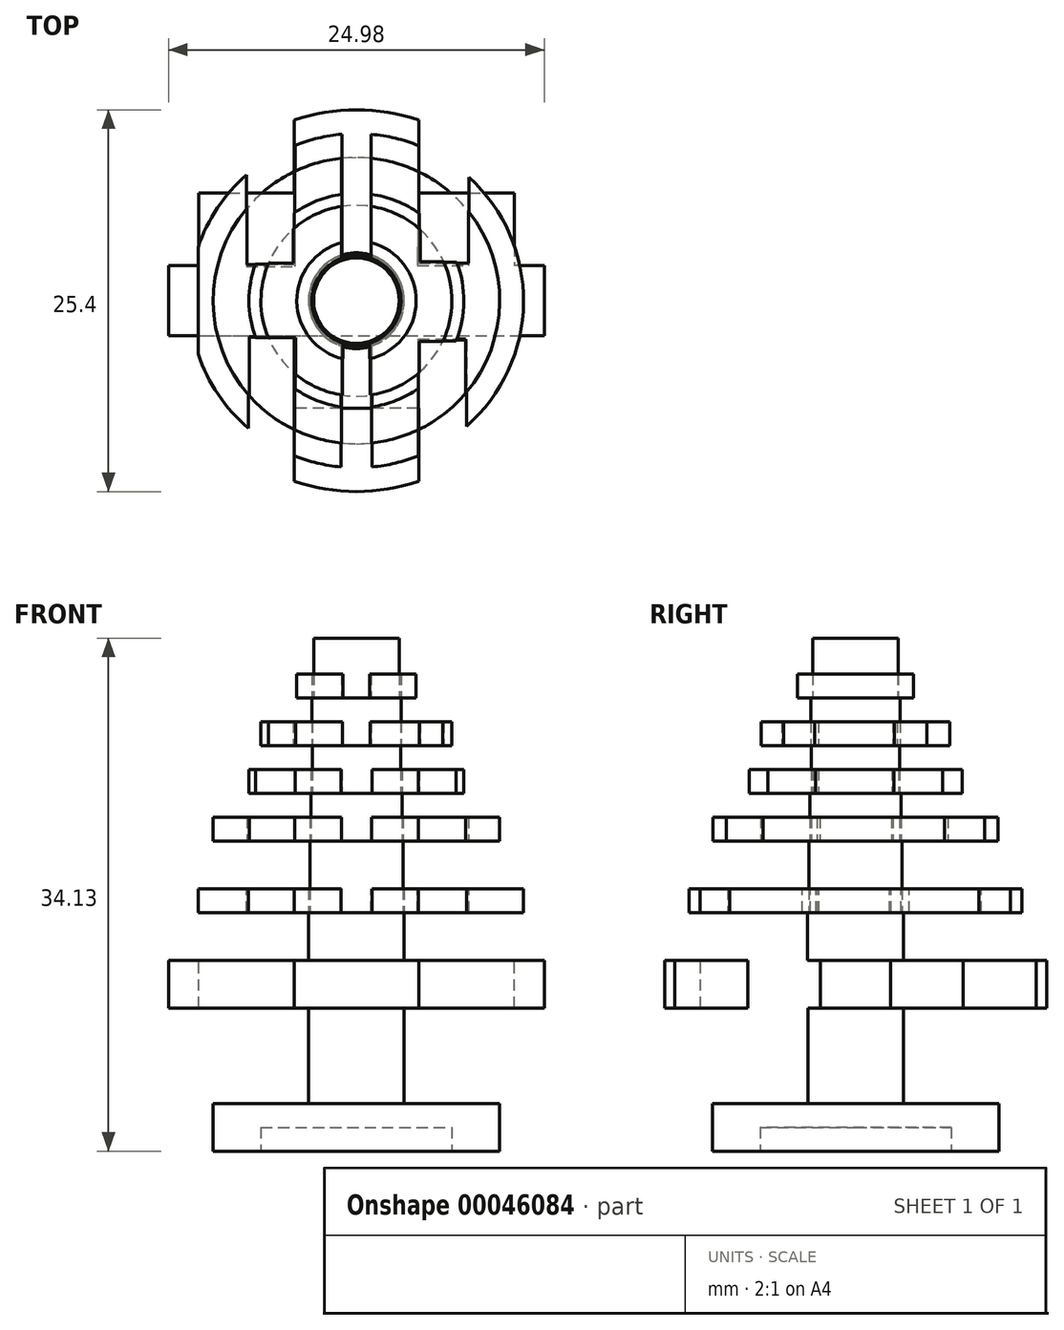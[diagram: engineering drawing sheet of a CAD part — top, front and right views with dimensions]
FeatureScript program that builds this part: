
annotation { "Feature Type Name" : "Feature", "Feature Type Description" : "" }
export const myFeature = defineFeature(function(context is Context, id is Id, definition is map)
    precondition{}
    {
        {
            var Q0;
            Q0=qCreatedBy(makeId("Top.planeOp"),FACE);
            var sketch = newSketch(context, id + "F0", { "sketchPlane" : qUnion([Q0])});
            skCircle(sketch, "E0", {"center": v(0, 0) * mm, "radius": 9.53 * mm});
            skSolve(sketch);
        }
        {
            var Q0;
            Q0=makeQuery(id+"F0.imprint","IMPRINT",FACE,{"disambiguationData":[TD([[makeQuery(id+"F0.imprint","IMPRINT",EDGE,{"derivedFrom":sQuery(id+"F0.wireOp",EDGE,"E0")}),1.0]])]});
            extrude(context, id + "F1", {"entities" : qUnion([Q0]), "depth" : 3.17 * mm});
        }
        {
            var Q0;
            Q0=makeQuery(id+"F1.opExtrude","CAP_FACE",FACE,{"disambiguationData":[OSD([sQuery(id+"F0.wireOp",EDGE,"E0")])],"isStart":false});
            var sketch = newSketch(context, id + "F2", { "sketchPlane" : qUnion([Q0])});
            skCircle(sketch, "E1", {"center": v(0, 0) * mm, "radius": 3.18 * mm});
            skSolve(sketch);
        }
        {
            var Q0;
            Q0=makeQuery(id+"F2.imprint","IMPRINT",FACE,{"disambiguationData":[TD([[makeQuery(id+"F2.imprint","IMPRINT",EDGE,{"derivedFrom":sQuery(id+"F2.wireOp",EDGE,"E1")}),1.0]])]});
            extrude(context, id + "F3", {"entities" : qUnion([Q0]), "depth" : 6.35 * mm});
        }
        {
            var Q0;
            Q0=makeQuery(id+"F1.opExtrude","CAP_FACE",FACE,{"disambiguationData":[OSD([sQuery(id+"F0.wireOp",EDGE,"E0")])],"isStart":true});
            var sketch = newSketch(context, id + "F4", { "sketchPlane" : qUnion([Q0])});
            skCircle(sketch, "E2", {"center": v(0, 0) * mm, "radius": 6.35 * mm});
            skSolve(sketch);
        }
        {
            var Q0;
            Q0=makeQuery(id+"F3.opExtrude","CAP_FACE",FACE,{"disambiguationData":[OSD([sQuery(id+"F2.wireOp",EDGE,"E1")])],"isStart":false});
            var sketch = newSketch(context, id + "F5", { "sketchPlane" : qUnion([Q0])});
            skCircle(sketch, "E3", {"center": v(0, 0) * mm, "radius": 12.7 * mm});
            skSolve(sketch);
        }
        {
            var Q0;
            Q0=makeQuery(id+"F5.imprint","IMPRINT",FACE,{"disambiguationData":[TD([[makeQuery(id+"F5.imprint","IMPRINT",EDGE,{"derivedFrom":makeQuery(id+"F3.opExtrude","CAP_EDGE",EDGE,{"disambiguationData":[OSD([sQuery(id+"F2.wireOp",EDGE,"E1")])],"isStart":false})}),1.0]])]});
            var Q1;
            Q1=makeQuery(id+"F5.imprint","IMPRINT",FACE,{"disambiguationData":[TD([[makeQuery(id+"F5.imprint","IMPRINT",EDGE,{"derivedFrom":sQuery(id+"F5.wireOp",EDGE,"E3")}),1.0]])]});
            extrude(context, id + "F6", {"entities" : qUnion([Q0, Q1]), "operationType" : NewBodyOperationType.ADD, "depth" : 3.17 * mm});
        }
        {
            var Q0;
            Q0=makeQuery(id+"F6.opExtrude","CAP_FACE",FACE,{"disambiguationData":[OSD([sQuery(id+"F5.wireOp",EDGE,"E3")])],"isStart":false});
            var sketch = newSketch(context, id + "F7", { "sketchPlane" : qUnion([Q0])});
            skLineSegment(sketch, "E4", {"start": v(10.49, 7.16) * mm, "end": v(10.49, -7.16) * mm});
            skLineSegment(sketch, "E5", {"start": v(10.49, -2.32) * mm, "end": v(12.49, -2.32) * mm});
            skLineSegment(sketch, "E6", {"start": v(12.49, -2.32) * mm, "end": v(12.49, 2.32) * mm});
            skLineSegment(sketch, "E7", {"start": v(12.49, 2.32) * mm, "end": v(10.49, 2.32) * mm});
            skLineSegment(sketch, "E8", {"start": v(10.49, 2.32) * mm, "end": v(-12.49, 2.32) * mm});
            skLineSegment(sketch, "E9", {"start": v(-12.49, 2.32) * mm, "end": v(-12.49, -2.32) * mm});
            skLineSegment(sketch, "E10", {"start": v(-12.49, -2.32) * mm, "end": v(10.49, -2.32) * mm});
            skLineSegment(sketch, "E11", {"start": v(10.49, -7.16) * mm, "end": v(-10.49, -7.16) * mm});
            skLineSegment(sketch, "E12", {"start": v(-10.49, -7.16) * mm, "end": v(-10.49, 7.16) * mm});
            skLineSegment(sketch, "E13", {"start": v(-10.49, 7.16) * mm, "end": v(10.49, 7.16) * mm});
            skLineSegment(sketch, "E14", {"start": v(-10.49, 2.32) * mm, "end": v(-12.49, 2.32) * mm});
            skLineSegment(sketch, "E15", {"start": v(-10.49, 7.16) * mm, "end": v(-7.31, 7.16) * mm});
            skLineSegment(sketch, "E16", {"start": v(-7.31, 7.16) * mm, "end": v(-7.31, 10.38) * mm});
            skLineSegment(sketch, "E17", {"start": v(-4.14, 12) * mm, "end": v(-4.14, 7.16) * mm});
            skLineSegment(sketch, "E18", {"start": v(-7.31, 7.16) * mm, "end": v(-4.14, 7.16) * mm});
            skLineSegment(sketch, "E19", {"start": v(10.49, 7.16) * mm, "end": v(7.31, 7.16) * mm});
            skLineSegment(sketch, "E20", {"start": v(7.31, 7.16) * mm, "end": v(7.31, 10.38) * mm});
            skLineSegment(sketch, "E21", {"start": v(7.31, 7.16) * mm, "end": v(4.14, 7.16) * mm});
            skLineSegment(sketch, "E22", {"start": v(4.14, 7.16) * mm, "end": v(4.14, 12) * mm});
            skLineSegment(sketch, "E23", {"start": v(-4.14, 7.16) * mm, "end": v(-0.96, 7.16) * mm});
            skLineSegment(sketch, "E24", {"start": v(-0.96, 7.16) * mm, "end": v(-0.96, 12.66) * mm});
            skLineSegment(sketch, "E25", {"start": v(4.14, 7.16) * mm, "end": v(0.96, 7.16) * mm});
            skLineSegment(sketch, "E26", {"start": v(0.96, 7.16) * mm, "end": v(0.96, 12.66) * mm});
            skLineSegment(sketch, "E27", {"start": v(-10.49, -7.16) * mm, "end": v(-7.31, -7.16) * mm});
            skLineSegment(sketch, "E28", {"start": v(-7.31, -7.16) * mm, "end": v(-7.31, -10.38) * mm});
            skLineSegment(sketch, "E29", {"start": v(-7.31, -7.16) * mm, "end": v(-4.14, -7.16) * mm});
            skLineSegment(sketch, "E30", {"start": v(-4.14, -7.16) * mm, "end": v(-4.14, -12) * mm});
            skLineSegment(sketch, "E31", {"start": v(-4.14, -7.16) * mm, "end": v(-0.96, -7.16) * mm});
            skLineSegment(sketch, "E32", {"start": v(-0.96, -7.16) * mm, "end": v(-0.96, -12.66) * mm});
            skLineSegment(sketch, "E33", {"start": v(10.49, -7.16) * mm, "end": v(7.31, -7.16) * mm});
            skLineSegment(sketch, "E34", {"start": v(7.31, -7.16) * mm, "end": v(7.31, -10.38) * mm});
            skLineSegment(sketch, "E35", {"start": v(7.31, -7.16) * mm, "end": v(4.14, -7.16) * mm});
            skLineSegment(sketch, "E36", {"start": v(4.14, -7.16) * mm, "end": v(4.14, -12) * mm});
            skLineSegment(sketch, "E37", {"start": v(4.14, -7.16) * mm, "end": v(0.96, -7.16) * mm});
            skLineSegment(sketch, "E38", {"start": v(0.96, -7.16) * mm, "end": v(0.96, -12.66) * mm});
            skLineSegment(sketch, "E39", {"start": v(-0.96, 7.16) * mm, "end": v(-0.96, 2.32) * mm});
            skLineSegment(sketch, "E40", {"start": v(-0.96, 2.32) * mm, "end": v(-4.14, 2.32) * mm});
            skLineSegment(sketch, "E41", {"start": v(-4.14, 2.32) * mm, "end": v(-4.14, 7.16) * mm});
            skLineSegment(sketch, "E42", {"start": v(-4.14, 2.32) * mm, "end": v(-7.31, 2.32) * mm});
            skLineSegment(sketch, "E43", {"start": v(-7.31, 2.32) * mm, "end": v(-7.31, 7.16) * mm});
            skLineSegment(sketch, "E44", {"start": v(-7.31, 2.32) * mm, "end": v(-10.49, 2.32) * mm});
            skLineSegment(sketch, "E45", {"start": v(0.96, 7.16) * mm, "end": v(0.96, 2.32) * mm});
            skLineSegment(sketch, "E46", {"start": v(0.96, 2.32) * mm, "end": v(4.14, 2.32) * mm});
            skLineSegment(sketch, "E47", {"start": v(4.14, 2.32) * mm, "end": v(4.14, 7.16) * mm});
            skLineSegment(sketch, "E48", {"start": v(4.14, 2.32) * mm, "end": v(7.31, 2.32) * mm});
            skLineSegment(sketch, "E49", {"start": v(7.31, 2.32) * mm, "end": v(7.31, 7.16) * mm});
            skLineSegment(sketch, "E50", {"start": v(7.31, 2.32) * mm, "end": v(10.49, 2.32) * mm});
            skLineSegment(sketch, "E51", {"start": v(7.31, -7.16) * mm, "end": v(7.31, -2.32) * mm});
            skLineSegment(sketch, "E52", {"start": v(4.14, -7.16) * mm, "end": v(4.14, -2.32) * mm});
            skLineSegment(sketch, "E53", {"start": v(0.96, -7.16) * mm, "end": v(0.96, -2.32) * mm});
            skLineSegment(sketch, "E54", {"start": v(-0.96, -7.16) * mm, "end": v(-0.96, -2.32) * mm});
            skLineSegment(sketch, "E55", {"start": v(-4.14, -7.16) * mm, "end": v(-4.14, -2.32) * mm});
            skLineSegment(sketch, "E56", {"start": v(-7.31, -7.16) * mm, "end": v(-7.31, -2.32) * mm});
            skSolve(sketch);
        }
        {
            var Q0;
            {var subQ1=sQuery(id+"F7.wireOp",EDGE,"E9");Q0=makeQuery(id+"F7.imprint","IMPRINT",FACE,{"disambiguationData":[TD([[makeQuery(id+"F7.imprint","IMPRINT",EDGE,{"derivedFrom":subQ1}),-1.0]])]});}
            var Q1;
            {var subQ3=sQuery(id+"F7.wireOp",EDGE,"E14");Q1=makeQuery(id+"F7.imprint","IMPRINT",FACE,{"disambiguationData":[TD([[makeQuery(id+"F7.imprint","IMPRINT",EDGE,{"derivedFrom":subQ3}),-1.0]])]});}
            var Q2;
            {var subQ1=sQuery(id+"F7.wireOp",EDGE,"E12");var subQ3=sQuery(id+"F7.wireOp",EDGE,"E10");var subQ5=makeQuery(id+"F7.imprint","INTERSECT",VERTEX,{"derivedFrom":[subQ3,subQ1]});Q2=makeQuery(id+"F7.imprint","IMPRINT",FACE,{"disambiguationData":[TD([[makeQuery(id+"F7.imprint","IMPRINT",EDGE,{"disambiguationData":[TD([[subQ5,1.0]])],"derivedFrom":subQ3}),-1.0]])]});}
            var Q3;
            {var subQ2=sQuery(id+"F7.wireOp",EDGE,"E28");Q3=makeQuery(id+"F7.imprint","IMPRINT",FACE,{"disambiguationData":[TD([[makeQuery(id+"F7.imprint","IMPRINT",EDGE,{"derivedFrom":subQ2}),1.0]])]});}
            var Q4;
            Q4=makeQuery(id+"F7.imprint","IMPRINT",FACE,{"disambiguationData":[TD([[makeQuery(id+"F7.imprint","IMPRINT",EDGE,{"derivedFrom":sQuery(id+"F7.wireOp",EDGE,"E29")}),1.0]])]});
            var Q5;
            Q5=makeQuery(id+"F7.imprint","IMPRINT",FACE,{"disambiguationData":[TD([[makeQuery(id+"F7.imprint","IMPRINT",EDGE,{"derivedFrom":sQuery(id+"F7.wireOp",EDGE,"E18")}),-1.0]])]});
            var Q6;
            {var subQ2=sQuery(id+"F7.wireOp",EDGE,"E16");Q6=makeQuery(id+"F7.imprint","IMPRINT",FACE,{"disambiguationData":[TD([[makeQuery(id+"F7.imprint","IMPRINT",EDGE,{"derivedFrom":subQ2}),-1.0]])]});}
            var Q7;
            Q7=makeQuery(id+"F7.imprint","IMPRINT",FACE,{"disambiguationData":[TD([[makeQuery(id+"F7.imprint","IMPRINT",EDGE,{"derivedFrom":sQuery(id+"F7.wireOp",EDGE,"E13")}),1.0]])]});
            var Q8;
            Q8=makeQuery(id+"F7.imprint","IMPRINT",FACE,{"disambiguationData":[TD([[makeQuery(id+"F7.imprint","IMPRINT",EDGE,{"derivedFrom":sQuery(id+"F7.wireOp",EDGE,"E8")}),-1.0]])]});
            var Q9;
            Q9=makeQuery(id+"F7.imprint","IMPRINT",FACE,{"disambiguationData":[TD([[makeQuery(id+"F7.imprint","IMPRINT",EDGE,{"derivedFrom":sQuery(id+"F7.wireOp",EDGE,"E11")}),-1.0]])]});
            var Q10;
            Q10=makeQuery(id+"F7.imprint","IMPRINT",FACE,{"disambiguationData":[TD([[makeQuery(id+"F7.imprint","IMPRINT",EDGE,{"derivedFrom":sQuery(id+"F7.wireOp",EDGE,"E11")}),1.0]])]});
            var Q11;
            {var subQ2=sQuery(id+"F7.wireOp",EDGE,"E34");Q11=makeQuery(id+"F7.imprint","IMPRINT",FACE,{"disambiguationData":[TD([[makeQuery(id+"F7.imprint","IMPRINT",EDGE,{"derivedFrom":subQ2}),-1.0]])]});}
            var Q12;
            Q12=makeQuery(id+"F7.imprint","IMPRINT",FACE,{"disambiguationData":[TD([[makeQuery(id+"F7.imprint","IMPRINT",EDGE,{"derivedFrom":sQuery(id+"F7.wireOp",EDGE,"E35")}),-1.0]])]});
            var Q13;
            {var subQ1=sQuery(id+"F7.wireOp",EDGE,"E5");Q13=makeQuery(id+"F7.imprint","IMPRINT",FACE,{"disambiguationData":[TD([[makeQuery(id+"F7.imprint","IMPRINT",EDGE,{"derivedFrom":subQ1}),-1.0]])]});}
            var Q14;
            {var subQ0=sQuery(id+"F7.wireOp",EDGE,"E7");Q14=makeQuery(id+"F7.imprint","IMPRINT",FACE,{"disambiguationData":[TD([[makeQuery(id+"F7.imprint","IMPRINT",EDGE,{"derivedFrom":subQ0}),-1.0]])]});}
            var Q15;
            Q15=makeQuery(id+"F7.imprint","IMPRINT",FACE,{"disambiguationData":[TD([[makeQuery(id+"F7.imprint","IMPRINT",EDGE,{"derivedFrom":sQuery(id+"F7.wireOp",EDGE,"E21")}),1.0]])]});
            var Q16;
            {var subQ2=sQuery(id+"F7.wireOp",EDGE,"E20");Q16=makeQuery(id+"F7.imprint","IMPRINT",FACE,{"disambiguationData":[TD([[makeQuery(id+"F7.imprint","IMPRINT",EDGE,{"derivedFrom":subQ2}),1.0]])]});}
            var Q17;
            {var subQ1=sQuery(id+"F7.wireOp",EDGE,"E6");Q17=makeQuery(id+"F7.imprint","IMPRINT",FACE,{"disambiguationData":[TD([[makeQuery(id+"F7.imprint","IMPRINT",EDGE,{"derivedFrom":subQ1}),-1.0]])]});}
            extrude(context, id + "F8", {"entities" : qUnion([Q0, Q1, Q2, Q3, Q4, Q5, Q6, Q7, Q8, Q9, Q10, Q11, Q12, Q13, Q14, Q15, Q16, Q17]), "operationType" : NewBodyOperationType.REMOVE, "oppositeDirection" : true, "depth" : 3.17 * mm});
        }
        {
            var Q0;
            Q0=makeQuery(id+"F7.imprint","IMPRINT",FACE,{"disambiguationData":[TD([[makeQuery(id+"F7.imprint","IMPRINT",EDGE,{"derivedFrom":sQuery(id+"F7.wireOp",EDGE,"E8")}),1.0]])]});
            var sketch = newSketch(context, id + "F9", { "sketchPlane" : qUnion([Q0])});
            skCircle(sketch, "E57", {"center": v(0, 0) * mm, "radius": 3.18 * mm});
            skSolve(sketch);
        }
        {
            var Q0;
            Q0 = qSketchRegion(id + "F9", true);
            extrude(context, id + "F10", {"entities" : qUnion([Q0]), "operationType" : NewBodyOperationType.ADD, "depth" : 3.17 * mm});
        }
        {
            var Q0;
            Q0=makeQuery(id+"F10.opExtrude","CAP_FACE",FACE,{"disambiguationData":[OSD([sQuery(id+"F9.wireOp",EDGE,"E57")])],"isStart":false});
            var sketch = newSketch(context, id + "F11", { "sketchPlane" : qUnion([Q0])});
            skCircle(sketch, "E58", {"center": v(0, 0) * mm, "radius": 11.11 * mm});
            skSolve(sketch);
        }
        {
            var Q0;
            Q0=makeQuery(id+"F11.imprint","IMPRINT",FACE,{"disambiguationData":[TD([[makeQuery(id+"F11.imprint","IMPRINT",EDGE,{"derivedFrom":sQuery(id+"F11.wireOp",EDGE,"E58")}),1.0]])]});
            extrude(context, id + "F12", {"entities" : qUnion([Q0]), "depth" : 1.59 * mm});
        }
        {
            var Q0;
            Q0=makeQuery(id+"F12.opExtrude","CAP_FACE",FACE,{"disambiguationData":[OSD([sQuery(id+"F9.wireOp",EDGE,"E57"),sQuery(id+"F11.wireOp",EDGE,"E58")])],"isStart":false});
            var sketch = newSketch(context, id + "F13", { "sketchPlane" : qUnion([Q0])});
            skLineSegment(sketch, "E59", {"start": v(-0.97, 3.03) * mm, "end": v(-0.97, 11.07) * mm});
            skLineSegment(sketch, "E60", {"start": v(-0.97, 11.07) * mm, "end": v(0.97, 11.07) * mm});
            skLineSegment(sketch, "E61", {"start": v(0.97, 11.07) * mm, "end": v(0.97, 3.03) * mm});
            skLineSegment(sketch, "E62", {"start": v(0.97, 3.03) * mm, "end": v(-0.97, 3.03) * mm});
            skLineSegment(sketch, "E63", {"start": v(4.06, 2.35) * mm, "end": v(7.5, 2.35) * mm});
            skLineSegment(sketch, "E64", {"start": v(7.5, 2.35) * mm, "end": v(7.5, 8.2) * mm});
            skLineSegment(sketch, "E65", {"start": v(7.5, 8.2) * mm, "end": v(4.16, 10.3) * mm});
            skLineSegment(sketch, "E66", {"start": v(4.16, 10.3) * mm, "end": v(4.06, 2.35) * mm});
            skLineSegment(sketch, "E67", {"start": v(10.59, 3.37) * mm, "end": v(10.59, -3.37) * mm});
            skLineSegment(sketch, "E68", {"start": v(-10.53, 3.55) * mm, "end": v(-10.53, -3.55) * mm});
            skLineSegment(sketch, "E69", {"start": v(-7.31, 8.37) * mm, "end": v(-7.31, 2.26) * mm});
            skLineSegment(sketch, "E70", {"start": v(-7.31, 2.26) * mm, "end": v(-4.08, 2.26) * mm});
            skLineSegment(sketch, "E71", {"start": v(-4.08, 2.26) * mm, "end": v(-4.08, 10.34) * mm});
            skLineSegment(sketch, "E72", {"start": v(-4.08, 10.34) * mm, "end": v(-7.31, 8.37) * mm});
            skLineSegment(sketch, "E73", {"start": v(-7.17, -2.44) * mm, "end": v(-7.17, -8.49) * mm});
            skLineSegment(sketch, "E74", {"start": v(-7.17, -8.49) * mm, "end": v(-4.13, -10.32) * mm});
            skLineSegment(sketch, "E75", {"start": v(-4.13, -10.32) * mm, "end": v(-4.13, -2.48) * mm});
            skLineSegment(sketch, "E76", {"start": v(-4.13, -2.48) * mm, "end": v(-7.17, -2.44) * mm});
            skLineSegment(sketch, "E77", {"start": v(-1.04, -2.53) * mm, "end": v(-1.04, -11.06) * mm});
            skLineSegment(sketch, "E78", {"start": v(-1.04, -11.06) * mm, "end": v(1.04, -11.06) * mm});
            skLineSegment(sketch, "E79", {"start": v(1.04, -11.06) * mm, "end": v(1.04, -3) * mm});
            skLineSegment(sketch, "E80", {"start": v(1.04, -3) * mm, "end": v(-1.04, -3) * mm});
            skLineSegment(sketch, "E81", {"start": v(4.11, -10.32) * mm, "end": v(4.11, -2.61) * mm});
            skLineSegment(sketch, "E82", {"start": v(4.11, -2.61) * mm, "end": v(7.32, -2.61) * mm});
            skLineSegment(sketch, "E83", {"start": v(7.32, -2.61) * mm, "end": v(7.32, -8.36) * mm});
            skLineSegment(sketch, "E84", {"start": v(7.32, -8.36) * mm, "end": v(4.11, -10.32) * mm});
            skSolve(sketch);
        }
        {
            var Q0;
            {var subQ1=sQuery(id+"F13.wireOp",EDGE,"E78");Q0=makeQuery(id+"F13.imprint","IMPRINT",FACE,{"disambiguationData":[TD([[makeQuery(id+"F13.imprint","IMPRINT",EDGE,{"derivedFrom":subQ1}),1.0]])]});}
            var Q1;
            Q1=makeQuery(id+"F13.imprint","IMPRINT",FACE,{"disambiguationData":[TD([[makeQuery(id+"F13.imprint","IMPRINT",EDGE,{"derivedFrom":sQuery(id+"F13.wireOp",EDGE,"E81")}),-1.0]])]});
            var Q2;
            Q2=makeQuery(id+"F13.imprint","IMPRINT",FACE,{"disambiguationData":[TD([[makeQuery(id+"F13.imprint","IMPRINT",EDGE,{"derivedFrom":sQuery(id+"F13.wireOp",EDGE,"E73")}),1.0]])]});
            var Q3;
            {var subQ1=sQuery(id+"F13.wireOp",EDGE,"E68");Q3=makeQuery(id+"F13.imprint","IMPRINT",FACE,{"disambiguationData":[TD([[makeQuery(id+"F13.imprint","IMPRINT",EDGE,{"derivedFrom":subQ1}),-1.0]])]});}
            var Q4;
            Q4=makeQuery(id+"F13.imprint","IMPRINT",FACE,{"disambiguationData":[TD([[makeQuery(id+"F13.imprint","IMPRINT",EDGE,{"derivedFrom":sQuery(id+"F13.wireOp",EDGE,"E69")}),1.0]])]});
            var Q5;
            {var subQ3=sQuery(id+"F13.wireOp",EDGE,"E59");Q5=makeQuery(id+"F13.imprint","IMPRINT",FACE,{"disambiguationData":[TD([[makeQuery(id+"F13.imprint","IMPRINT",EDGE,{"derivedFrom":subQ3}),-1.0]])]});}
            var Q6;
            Q6=makeQuery(id+"F13.imprint","IMPRINT",FACE,{"disambiguationData":[TD([[makeQuery(id+"F13.imprint","IMPRINT",EDGE,{"derivedFrom":sQuery(id+"F13.wireOp",EDGE,"E63")}),1.0]])]});
            var Q7;
            {var subQ1=sQuery(id+"F13.wireOp",EDGE,"E65");Q7=makeQuery(id+"F13.imprint","IMPRINT",FACE,{"disambiguationData":[TD([[makeQuery(id+"F13.imprint","IMPRINT",EDGE,{"derivedFrom":subQ1}),-1.0]])]});}
            var Q8;
            {var subQ1=sQuery(id+"F13.wireOp",EDGE,"E78");Q8=makeQuery(id+"F13.imprint","IMPRINT",FACE,{"disambiguationData":[TD([[makeQuery(id+"F13.imprint","IMPRINT",EDGE,{"derivedFrom":subQ1}),-1.0]])]});}
            var Q9;
            {var subQ1=sQuery(id+"F13.wireOp",EDGE,"E84");Q9=makeQuery(id+"F13.imprint","IMPRINT",FACE,{"disambiguationData":[TD([[makeQuery(id+"F13.imprint","IMPRINT",EDGE,{"derivedFrom":subQ1}),1.0]])]});}
            var Q10;
            {var subQ1=sQuery(id+"F13.wireOp",EDGE,"E72");Q10=makeQuery(id+"F13.imprint","IMPRINT",FACE,{"disambiguationData":[TD([[makeQuery(id+"F13.imprint","IMPRINT",EDGE,{"derivedFrom":subQ1}),-1.0]])]});}
            var Q11;
            {var subQ1=sQuery(id+"F13.wireOp",EDGE,"E60");Q11=makeQuery(id+"F13.imprint","IMPRINT",FACE,{"disambiguationData":[TD([[makeQuery(id+"F13.imprint","IMPRINT",EDGE,{"derivedFrom":subQ1}),1.0]])]});}
            extrude(context, id + "F14", {"entities" : qUnion([Q0, Q1, Q2, Q3, Q4, Q5, Q6, Q7, Q8, Q9, Q10, Q11]), "operationType" : NewBodyOperationType.REMOVE, "oppositeDirection" : true, "depth" : 1.59 * mm});
        }
        {
            var Q0;
            Q0=makeQuery(id+"F4.imprint","IMPRINT",FACE,{"disambiguationData":[TD([[makeQuery(id+"F4.imprint","IMPRINT",EDGE,{"derivedFrom":sQuery(id+"F4.wireOp",EDGE,"E2")}),1.0]])]});
            extrude(context, id + "F15", {"entities" : qUnion([Q0]), "operationType" : NewBodyOperationType.REMOVE, "oppositeDirection" : true, "depth" : 1.59 * mm});
        }
        {
            var Q0;
            Q0=makeQuery(id+"F10.opExtrude","CAP_FACE",FACE,{"disambiguationData":[OSD([sQuery(id+"F9.wireOp",EDGE,"E57")])],"isStart":false});
            var sketch = newSketch(context, id + "F16", { "sketchPlane" : qUnion([Q0])});
            skCircle(sketch, "E85", {"center": v(0, 0) * mm, "radius": 3.1 * mm});
            skSolve(sketch);
        }
        {
            var Q0;
            Q0=makeQuery(id+"F16.imprint","IMPRINT",FACE,{"disambiguationData":[TD([[makeQuery(id+"F16.imprint","IMPRINT",EDGE,{"derivedFrom":sQuery(id+"F16.wireOp",EDGE,"E85")}),1.0]])]});
            extrude(context, id + "F17", {"entities" : qUnion([Q0]), "depth" : 4.76 * mm});
        }
        {
            var Q0;
            {var subQ0=sQuery(id+"F11.wireOp",EDGE,"E58");Q0=makeQuery(id+"F14.boolean.opBoolean","SPLIT",FACE,{"disambiguationData":[TD([makeQuery(id+"F14.opExtrude","SWEPT_FACE",FACE,{"disambiguationData":[OSD([sQuery(id+"F13.wireOp",EDGE,"E74")])]})])],"derivedFrom":makeQuery(id+"F12.opExtrude","CAP_FACE",FACE,{"disambiguationData":[OSD([sQuery(id+"F9.wireOp",EDGE,"E57"),subQ0])],"isStart":false})});}
            extrude(context, id + "F18", {"entities" : qUnion([Q0]), "operationType" : NewBodyOperationType.REMOVE, "oppositeDirection" : true, "depth" : 25.4 * mm});
        }
        {
            var Q0;
            Q0=makeQuery(id+"F17.opExtrude","CAP_FACE",FACE,{"disambiguationData":[OSD([sQuery(id+"F16.wireOp",EDGE,"E85")])],"isStart":false});
            var sketch = newSketch(context, id + "F19", { "sketchPlane" : qUnion([Q0])});
            skCircle(sketch, "E86", {"center": v(0, 0) * mm, "radius": 9.53 * mm});
            skLineSegment(sketch, "E87", {"start": v(-0.98, 9.47) * mm, "end": v(-0.98, 2.94) * mm});
            skLineSegment(sketch, "E88", {"start": v(-0.98, 2.94) * mm, "end": v(0.98, 2.94) * mm});
            skLineSegment(sketch, "E89", {"start": v(0.98, 2.94) * mm, "end": v(0.98, 9.47) * mm});
            skLineSegment(sketch, "E90", {"start": v(0.98, 9.47) * mm, "end": v(-0.98, 9.47) * mm});
            skLineSegment(sketch, "E91", {"start": v(4.15, 8.57) * mm, "end": v(4.15, 2.48) * mm});
            skLineSegment(sketch, "E92", {"start": v(4.15, 2.48) * mm, "end": v(7.46, 2.48) * mm});
            skLineSegment(sketch, "E93", {"start": v(7.46, 2.48) * mm, "end": v(7.46, 5.92) * mm});
            skLineSegment(sketch, "E94", {"start": v(-4.1, 8.6) * mm, "end": v(-4.1, 2.39) * mm});
            skLineSegment(sketch, "E95", {"start": v(-4.1, 2.39) * mm, "end": v(-7.28, 2.39) * mm});
            skLineSegment(sketch, "E96", {"start": v(-7.28, 2.39) * mm, "end": v(-7.28, 6.14) * mm});
            skLineSegment(sketch, "E97", {"start": v(-7.12, -6.32) * mm, "end": v(-7.12, -2.38) * mm});
            skLineSegment(sketch, "E98", {"start": v(-7.12, -2.38) * mm, "end": v(-4.11, -2.38) * mm});
            skLineSegment(sketch, "E99", {"start": v(-4.11, -2.38) * mm, "end": v(-4.11, -8.6) * mm});
            skLineSegment(sketch, "E100", {"start": v(-1, -9.47) * mm, "end": v(-1, -2.93) * mm});
            skLineSegment(sketch, "E101", {"start": v(-1, -2.93) * mm, "end": v(1, -2.93) * mm});
            skLineSegment(sketch, "E102", {"start": v(1, -2.93) * mm, "end": v(1, -9.47) * mm});
            skLineSegment(sketch, "E103", {"start": v(4.11, -8.6) * mm, "end": v(4.11, -2.57) * mm});
            skLineSegment(sketch, "E104", {"start": v(4.11, -2.57) * mm, "end": v(7.27, -2.57) * mm});
            skLineSegment(sketch, "E105", {"start": v(7.27, -2.57) * mm, "end": v(7.27, -6.15) * mm});
            skSolve(sketch);
        }
        {
            var Q0;
            {var subQ5=sQuery(id+"F19.wireOp",EDGE,"E89");Q0=makeQuery(id+"F19.imprint","IMPRINT",FACE,{"disambiguationData":[TD([[makeQuery(id+"F19.imprint","IMPRINT",EDGE,{"derivedFrom":subQ5}),-1.0]])]});}
            var Q1;
            {var subQ5=sQuery(id+"F19.wireOp",EDGE,"E87");Q1=makeQuery(id+"F19.imprint","IMPRINT",FACE,{"disambiguationData":[TD([[makeQuery(id+"F19.imprint","IMPRINT",EDGE,{"derivedFrom":subQ5}),-1.0]])]});}
            extrude(context, id + "F20", {"entities" : qUnion([Q0, Q1]), "depth" : 1.59 * mm});
        }
        {
            var Q0;
            Q0=makeQuery(id+"F17.opExtrude","CAP_FACE",FACE,{"disambiguationData":[OSD([sQuery(id+"F16.wireOp",EDGE,"E85")])],"isStart":false});
            var sketch = newSketch(context, id + "F21", { "sketchPlane" : qUnion([Q0])});
            skCircle(sketch, "E106", {"center": v(0, 0) * mm, "radius": 3.04 * mm});
            skSolve(sketch);
        }
        {
            var Q0;
            Q0=makeQuery(id+"F21.imprint","IMPRINT",FACE,{"disambiguationData":[TD([[makeQuery(id+"F21.imprint","IMPRINT",EDGE,{"derivedFrom":sQuery(id+"F21.wireOp",EDGE,"E106")}),1.0]])]});
            extrude(context, id + "F22", {"entities" : qUnion([Q0]), "operationType" : NewBodyOperationType.ADD, "depth" : 3.17 * mm});
        }
        {
            var Q0;
            Q0=makeQuery(id+"F22.opExtrude","CAP_FACE",FACE,{"disambiguationData":[OSD([sQuery(id+"F21.wireOp",EDGE,"E106")])],"isStart":false});
            var sketch = newSketch(context, id + "F23", { "sketchPlane" : qUnion([Q0])});
            skCircle(sketch, "E107", {"center": v(0, 0) * mm, "radius": 7.14 * mm});
            skLineSegment(sketch, "E108", {"start": v(-4.14, 5.82) * mm, "end": v(-4.14, 2.42) * mm});
            skLineSegment(sketch, "E109", {"start": v(-4.14, 2.42) * mm, "end": v(-6.72, 2.42) * mm});
            skLineSegment(sketch, "E110", {"start": v(-0.97, 7.08) * mm, "end": v(-0.97, 2.88) * mm});
            skLineSegment(sketch, "E111", {"start": v(-0.97, 2.88) * mm, "end": v(0.97, 2.88) * mm});
            skLineSegment(sketch, "E112", {"start": v(0.97, 2.88) * mm, "end": v(0.97, 7.08) * mm});
            skLineSegment(sketch, "E113", {"start": v(4.18, 5.8) * mm, "end": v(4.18, 2.55) * mm});
            skLineSegment(sketch, "E114", {"start": v(4.18, 2.55) * mm, "end": v(6.67, 2.55) * mm});
            skLineSegment(sketch, "E115", {"start": v(4.13, -5.83) * mm, "end": v(4.13, -2.67) * mm});
            skLineSegment(sketch, "E116", {"start": v(4.13, -2.67) * mm, "end": v(6.63, -2.67) * mm});
            skLineSegment(sketch, "E117", {"start": v(1.03, -7.07) * mm, "end": v(1.03, -2.86) * mm});
            skLineSegment(sketch, "E118", {"start": v(1.03, -2.86) * mm, "end": v(-1.03, -2.86) * mm});
            skLineSegment(sketch, "E119", {"start": v(-1.03, -2.86) * mm, "end": v(-1.03, -7.07) * mm});
            skLineSegment(sketch, "E120", {"start": v(-4.08, -5.86) * mm, "end": v(-4.08, -2.45) * mm});
            skLineSegment(sketch, "E121", {"start": v(-4.08, -2.45) * mm, "end": v(-6.71, -2.45) * mm});
            skSolve(sketch);
        }
        {
            var Q0;
            {var subQ0=sQuery(id+"F23.wireOp",EDGE,"E108");Q0=makeQuery(id+"F23.imprint","IMPRINT",FACE,{"disambiguationData":[TD([[makeQuery(id+"F23.imprint","IMPRINT",EDGE,{"derivedFrom":subQ0}),1.0]])]});}
            var Q1;
            {var subQ0=sQuery(id+"F23.wireOp",EDGE,"E112");Q1=makeQuery(id+"F23.imprint","IMPRINT",FACE,{"disambiguationData":[TD([[makeQuery(id+"F23.imprint","IMPRINT",EDGE,{"derivedFrom":subQ0}),-1.0]])]});}
            extrude(context, id + "F24", {"entities" : qUnion([Q0, Q1]), "depth" : 1.59 * mm});
        }
        {
            var Q0;
            Q0=makeQuery(id+"F22.opExtrude","CAP_FACE",FACE,{"disambiguationData":[OSD([sQuery(id+"F21.wireOp",EDGE,"E106")])],"isStart":false});
            var sketch = newSketch(context, id + "F25", { "sketchPlane" : qUnion([Q0])});
            skCircle(sketch, "E122", {"center": v(0, 0) * mm, "radius": 2.94 * mm});
            skSolve(sketch);
        }
        {
            var Q0;
            Q0=makeQuery(id+"F25.imprint","IMPRINT",FACE,{"disambiguationData":[TD([[makeQuery(id+"F25.imprint","IMPRINT",EDGE,{"derivedFrom":sQuery(id+"F25.wireOp",EDGE,"E122")}),1.0]])]});
            extrude(context, id + "F26", {"entities" : qUnion([Q0]), "operationType" : NewBodyOperationType.ADD, "depth" : 3.17 * mm});
        }
        {
            var Q0;
            Q0=makeQuery(id+"F26.opExtrude","CAP_FACE",FACE,{"disambiguationData":[OSD([sQuery(id+"F25.wireOp",EDGE,"E122")])],"isStart":false});
            var sketch = newSketch(context, id + "F27", { "sketchPlane" : qUnion([Q0])});
            skCircle(sketch, "E123", {"center": v(0, 0) * mm, "radius": 6.35 * mm});
            skLineSegment(sketch, "E124", {"start": v(-0.98, 6.27) * mm, "end": v(-0.98, 2.77) * mm});
            skLineSegment(sketch, "E125", {"start": v(-0.98, 2.77) * mm, "end": v(0.98, 2.77) * mm});
            skLineSegment(sketch, "E126", {"start": v(0.98, 2.77) * mm, "end": v(0.98, 6.27) * mm});
            skLineSegment(sketch, "E127", {"start": v(4.23, 4.73) * mm, "end": v(4.23, 2.58) * mm});
            skLineSegment(sketch, "E128", {"start": v(4.23, 2.58) * mm, "end": v(5.8, 2.58) * mm});
            skLineSegment(sketch, "E129", {"start": v(5.85, -2.7) * mm, "end": v(4.19, -2.7) * mm});
            skLineSegment(sketch, "E130", {"start": v(4.19, -2.7) * mm, "end": v(4.19, -4.99) * mm});
            skLineSegment(sketch, "E131", {"start": v(-0.92, -6.28) * mm, "end": v(-0.92, -2.8) * mm});
            skLineSegment(sketch, "E132", {"start": v(-0.92, -2.8) * mm, "end": v(0.92, -2.8) * mm});
            skLineSegment(sketch, "E133", {"start": v(0.92, -2.8) * mm, "end": v(0.92, -6.28) * mm});
            skLineSegment(sketch, "E134", {"start": v(-4.04, -4.9) * mm, "end": v(-4.04, -2.46) * mm});
            skLineSegment(sketch, "E135", {"start": v(-4.04, -2.46) * mm, "end": v(-5.85, -2.46) * mm});
            skLineSegment(sketch, "E136", {"start": v(-5.84, 2.49) * mm, "end": v(-4.19, 2.49) * mm});
            skLineSegment(sketch, "E137", {"start": v(-4.19, 2.49) * mm, "end": v(-4.19, 4.78) * mm});
            skSolve(sketch);
        }
        {
            var Q0;
            {var subQ0=sQuery(id+"F27.wireOp",EDGE,"E124");Q0=makeQuery(id+"F27.imprint","IMPRINT",FACE,{"disambiguationData":[TD([[makeQuery(id+"F27.imprint","IMPRINT",EDGE,{"derivedFrom":subQ0}),-1.0]])]});}
            var Q1;
            {var subQ0=sQuery(id+"F27.wireOp",EDGE,"E126");Q1=makeQuery(id+"F27.imprint","IMPRINT",FACE,{"disambiguationData":[TD([[makeQuery(id+"F27.imprint","IMPRINT",EDGE,{"derivedFrom":subQ0}),-1.0]])]});}
            extrude(context, id + "F28", {"entities" : qUnion([Q0, Q1]), "depth" : 1.59 * mm});
        }
        {
            var Q0;
            Q0=makeQuery(id+"F26.opExtrude","CAP_FACE",FACE,{"disambiguationData":[OSD([sQuery(id+"F25.wireOp",EDGE,"E122")])],"isStart":false});
            var sketch = newSketch(context, id + "F29", { "sketchPlane" : qUnion([Q0])});
            skCircle(sketch, "E138", {"center": v(0, 0) * mm, "radius": 2.96 * mm});
            skSolve(sketch);
        }
        {
            var Q0;
            Q0 = qSketchRegion(id + "F29", true);
            extrude(context, id + "F30", {"entities" : qUnion([Q0]), "depth" : 3.17 * mm});
        }
        {
            var Q0;
            Q0=makeQuery(id+"F30.opExtrude","CAP_FACE",FACE,{"disambiguationData":[OSD([sQuery(id+"F29.wireOp",EDGE,"E138")])],"isStart":false});
            var sketch = newSketch(context, id + "F31", { "sketchPlane" : qUnion([Q0])});
            skCircle(sketch, "E139", {"center": v(0, 0) * mm, "radius": 3.97 * mm});
            skLineSegment(sketch, "E140", {"start": v(-0.98, 3.85) * mm, "end": v(-0.98, 2.8) * mm});
            skLineSegment(sketch, "E141", {"start": v(-0.98, 2.8) * mm, "end": v(0.98, 2.8) * mm});
            skLineSegment(sketch, "E142", {"start": v(0.98, 2.8) * mm, "end": v(0.98, 3.85) * mm});
            skLineSegment(sketch, "E143", {"start": v(-0.88, -3.87) * mm, "end": v(-0.88, -2.83) * mm});
            skLineSegment(sketch, "E144", {"start": v(-0.88, -2.83) * mm, "end": v(0.88, -2.83) * mm});
            skLineSegment(sketch, "E145", {"start": v(0.88, -2.83) * mm, "end": v(0.88, -3.87) * mm});
            skSolve(sketch);
        }
        {
            var Q0;
            {var subQ0=sQuery(id+"F31.wireOp",EDGE,"E142");Q0=makeQuery(id+"F31.imprint","IMPRINT",FACE,{"disambiguationData":[TD([[makeQuery(id+"F31.imprint","IMPRINT",EDGE,{"derivedFrom":subQ0}),-1.0]])]});}
            var Q1;
            {var subQ0=sQuery(id+"F31.wireOp",EDGE,"E140");Q1=makeQuery(id+"F31.imprint","IMPRINT",FACE,{"disambiguationData":[TD([[makeQuery(id+"F31.imprint","IMPRINT",EDGE,{"derivedFrom":subQ0}),-1.0]])]});}
            extrude(context, id + "F32", {"entities" : qUnion([Q0, Q1]), "depth" : 1.59 * mm});
        }
        {
            var Q0;
            Q0=makeQuery(id+"F30.opExtrude","CAP_FACE",FACE,{"disambiguationData":[OSD([sQuery(id+"F29.wireOp",EDGE,"E138")])],"isStart":false});
            var sketch = newSketch(context, id + "F33", { "sketchPlane" : qUnion([Q0])});
            skCircle(sketch, "E146", {"center": v(0, 0) * mm, "radius": 2.85 * mm});
            skSolve(sketch);
        }
        {
            var Q0;
            Q0=makeQuery(id+"F33.imprint","IMPRINT",FACE,{"disambiguationData":[TD([[makeQuery(id+"F33.imprint","IMPRINT",EDGE,{"derivedFrom":sQuery(id+"F33.wireOp",EDGE,"E146")}),1.0]])]});
            extrude(context, id + "F34", {"entities" : qUnion([Q0]), "operationType" : NewBodyOperationType.ADD, "depth" : 3.97 * mm});
        }
    });
